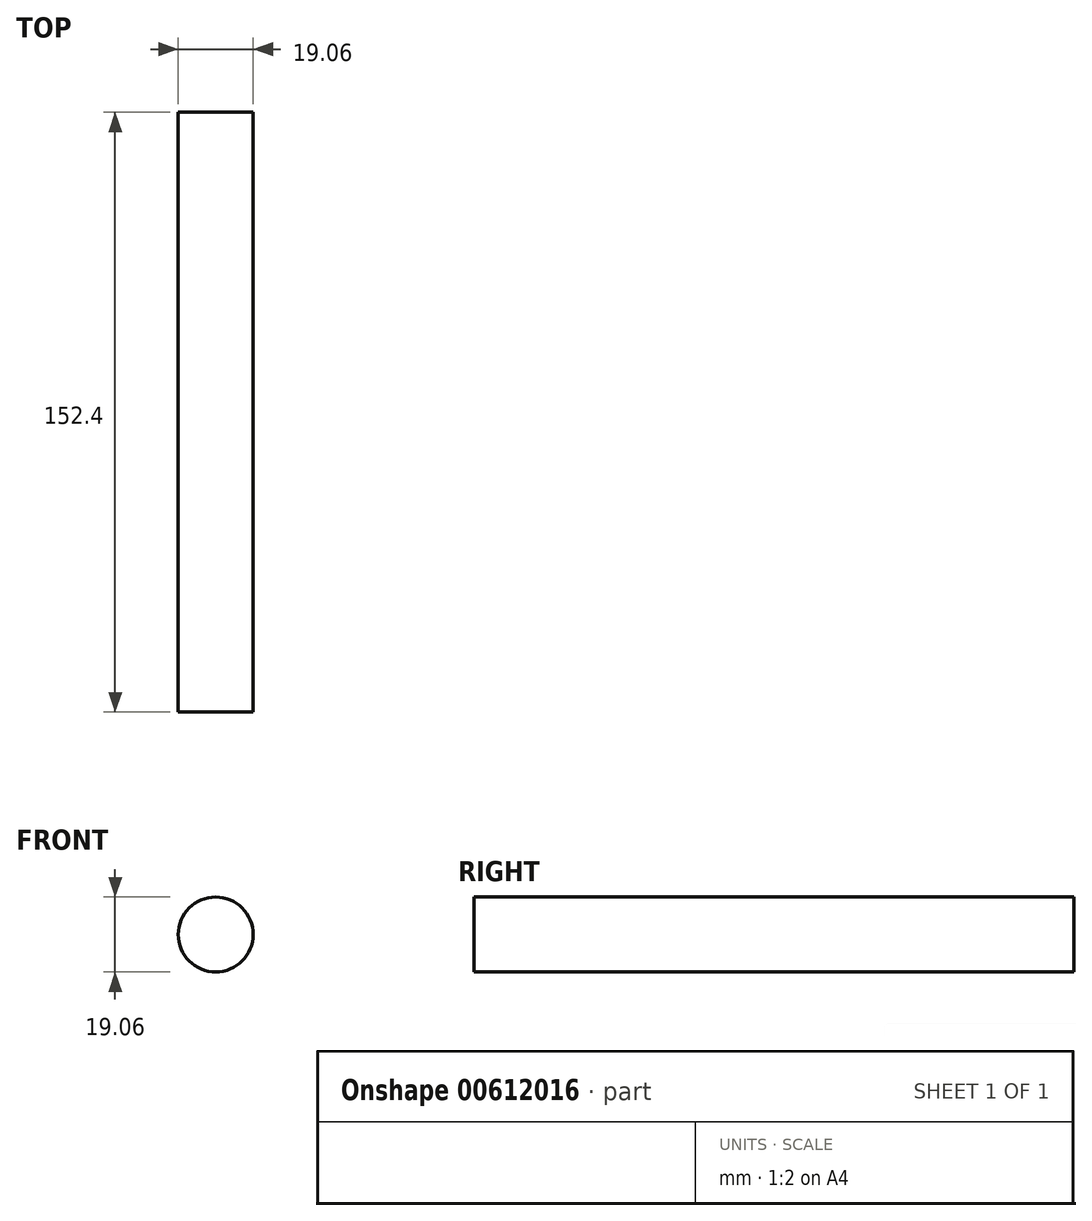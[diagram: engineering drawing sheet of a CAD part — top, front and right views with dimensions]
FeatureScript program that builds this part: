
annotation { "Feature Type Name" : "Feature", "Feature Type Description" : "" }
export const myFeature = defineFeature(function(context is Context, id is Id, definition is map)
    precondition{}
    {
        {
            var Q0;
            Q0=qCreatedBy(makeId("Front.planeOp"),FACE);
            var sketch = newSketch(context, id + "F0", { "sketchPlane" : qUnion([Q0])});
            skCircle(sketch, "E0", {"center": v(0, 0) * mm, "radius": 9.53 * mm});
            skSolve(sketch);
        }
        {
            var Q0;
            Q0=makeQuery(id+"F0.imprint","IMPRINT",FACE,{"disambiguationData":[TD([[makeQuery(id+"F0.imprint","IMPRINT",EDGE,{"derivedFrom":sQuery(id+"F0.wireOp",EDGE,"E0")}),1.0]])]});
            extrude(context, id + "F1", {"entities" : qUnion([Q0]), "depth" : 152.4 * mm, "offsetDistance" : 25.4 * mm});
        }
    });
